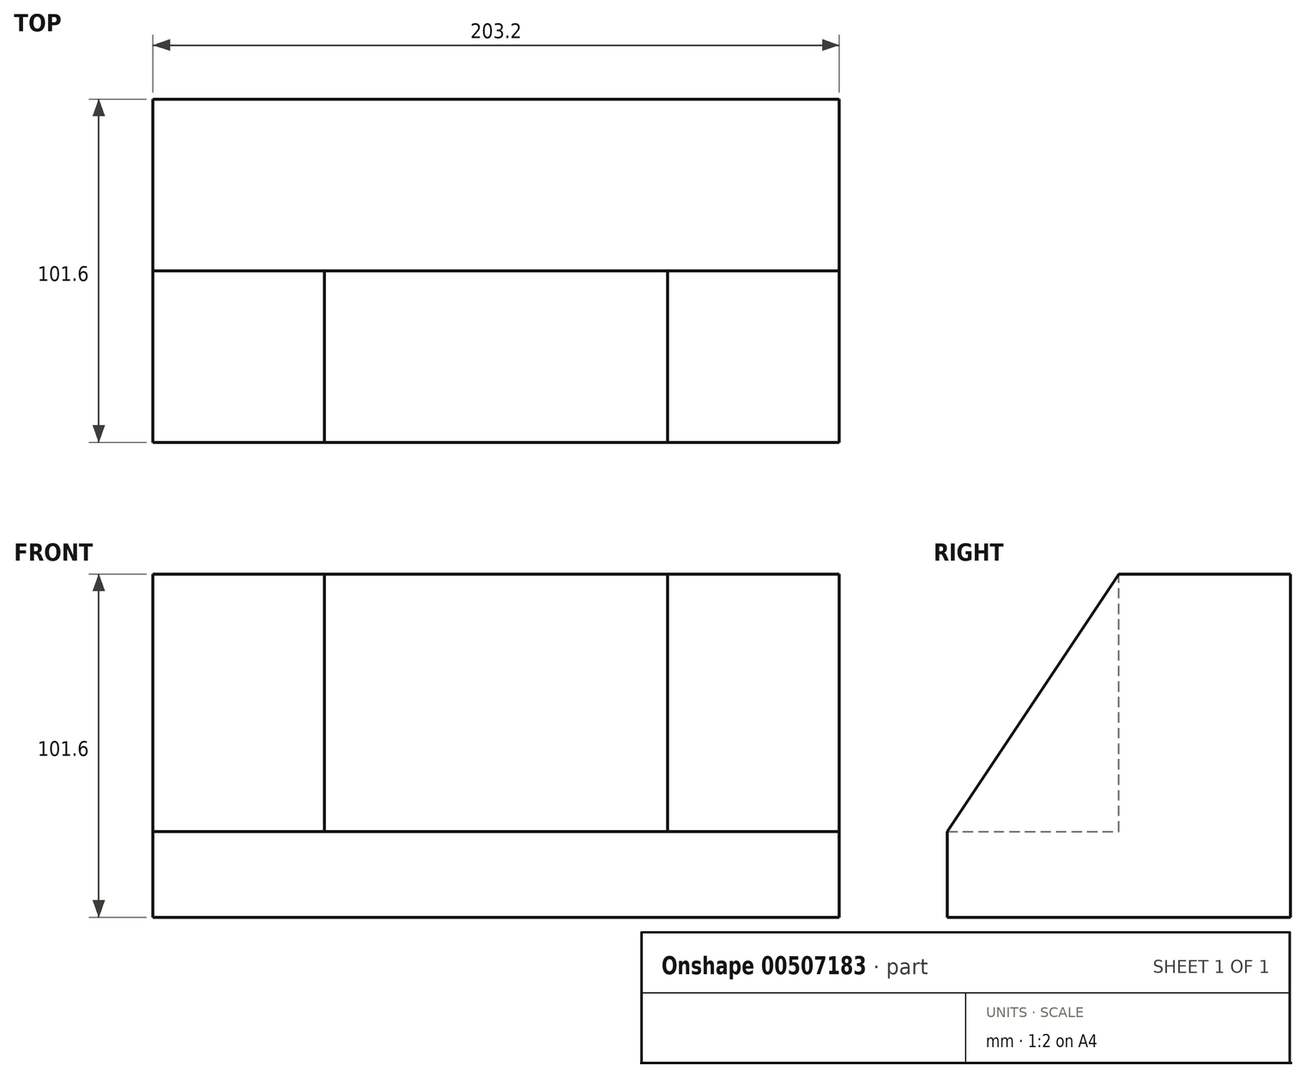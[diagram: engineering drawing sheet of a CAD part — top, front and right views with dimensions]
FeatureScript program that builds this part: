
annotation { "Feature Type Name" : "Feature", "Feature Type Description" : "" }
export const myFeature = defineFeature(function(context is Context, id is Id, definition is map)
    precondition{}
    {
        {
            var Q0;
            Q0=qCreatedBy(makeId("Top.planeOp"),FACE);
            var sketch = newSketch(context, id + "F0", { "sketchPlane" : qUnion([Q0])});
            skLineSegment(sketch, "E0.bottom", {"start": v(0, 0) * mm, "end": v(203.2, 0) * mm});
            skLineSegment(sketch, "E0.top", {"start": v(0, -101.6) * mm, "end": v(203.2, -101.6) * mm});
            skLineSegment(sketch, "E0.left", {"start": v(0, 0) * mm, "end": v(0, -101.6) * mm});
            skLineSegment(sketch, "E0.right", {"start": v(203.2, 0) * mm, "end": v(203.2, -101.6) * mm});
            skSolve(sketch);
        }
        {
            var Q0;
            Q0=makeQuery(id+"F0.imprint","IMPRINT",FACE,{"disambiguationData":[TD([[makeQuery(id+"F0.imprint","IMPRINT",EDGE,{"derivedFrom":sQuery(id+"F0.wireOp",EDGE,"E0.bottom")}),-1.0]])]});
            extrude(context, id + "F1", {"entities" : qUnion([Q0]), "depth" : 101.6 * mm});
        }
        {
            var Q0;
            Q0=makeQuery(id+"F1.opExtrude","CAP_FACE",FACE,{"disambiguationData":[OSD([sQuery(id+"F0.wireOp",EDGE,"E0.bottom"),sQuery(id+"F0.wireOp",EDGE,"E0.top"),sQuery(id+"F0.wireOp",EDGE,"E0.left"),sQuery(id+"F0.wireOp",EDGE,"E0.right")])],"isStart":false});
            var sketch = newSketch(context, id + "F2", { "sketchPlane" : qUnion([Q0])});
            skLineSegment(sketch, "E1.bottom", {"start": v(50.8, -101.6) * mm, "end": v(152.4, -101.6) * mm});
            skLineSegment(sketch, "E1.top", {"start": v(50.8, -50.8) * mm, "end": v(152.4, -50.8) * mm});
            skLineSegment(sketch, "E1.left", {"start": v(50.8, -101.6) * mm, "end": v(50.8, -50.8) * mm});
            skLineSegment(sketch, "E1.right", {"start": v(152.4, -101.6) * mm, "end": v(152.4, -50.8) * mm});
            skSolve(sketch);
        }
        {
            var Q0;
            Q0=makeQuery(id+"F2.imprint","IMPRINT",FACE,{"disambiguationData":[TD([[makeQuery(id+"F2.imprint","IMPRINT",EDGE,{"derivedFrom":sQuery(id+"F2.wireOp",EDGE,"E1.bottom")}),1.0]])]});
            extrude(context, id + "F3", {"entities" : qUnion([Q0]), "operationType" : NewBodyOperationType.REMOVE, "oppositeDirection" : true, "depth" : 76.2 * mm});
        }
        {
            var Q0;
            {var subQ0=sQuery(id+"F0.wireOp",EDGE,"E0.right");var subQ1=sQuery(id+"F0.wireOp",EDGE,"E0.top");Q0=makeQuery(id+"F3.boolean.opBoolean","SPLIT",EDGE,{"disambiguationData":[TD([makeQuery(id+"F1.opExtrude","SWEPT_FACE",FACE,{"disambiguationData":[OSD([subQ0])]})])],"derivedFrom":makeQuery(id+"F1.opExtrude","CAP_EDGE",EDGE,{"disambiguationData":[OSD([subQ1])],"isStart":false})});}
            chamfer(context, id + "F4", {"entities" : qUnion([Q0]), "chamferType" : ChamferType.TWO_OFFSETS, "width1" : 50.8 * mm, "oppositeDirection" : false, "width2" : 76.2 * mm, "tangentPropagation" : true});
        }
        {
            var Q0;
            {var subQ0=sQuery(id+"F0.wireOp",EDGE,"E0.left");var subQ1=sQuery(id+"F0.wireOp",EDGE,"E0.top");Q0=makeQuery(id+"F3.boolean.opBoolean","SPLIT",EDGE,{"disambiguationData":[TD([makeQuery(id+"F1.opExtrude","SWEPT_FACE",FACE,{"disambiguationData":[OSD([subQ0])]})])],"derivedFrom":makeQuery(id+"F1.opExtrude","CAP_EDGE",EDGE,{"disambiguationData":[OSD([subQ1])],"isStart":false})});}
            chamfer(context, id + "F5", {"entities" : qUnion([Q0]), "chamferType" : ChamferType.TWO_OFFSETS, "width1" : 50.8 * mm, "oppositeDirection" : false, "width2" : 76.2 * mm, "tangentPropagation" : true});
        }
    });
